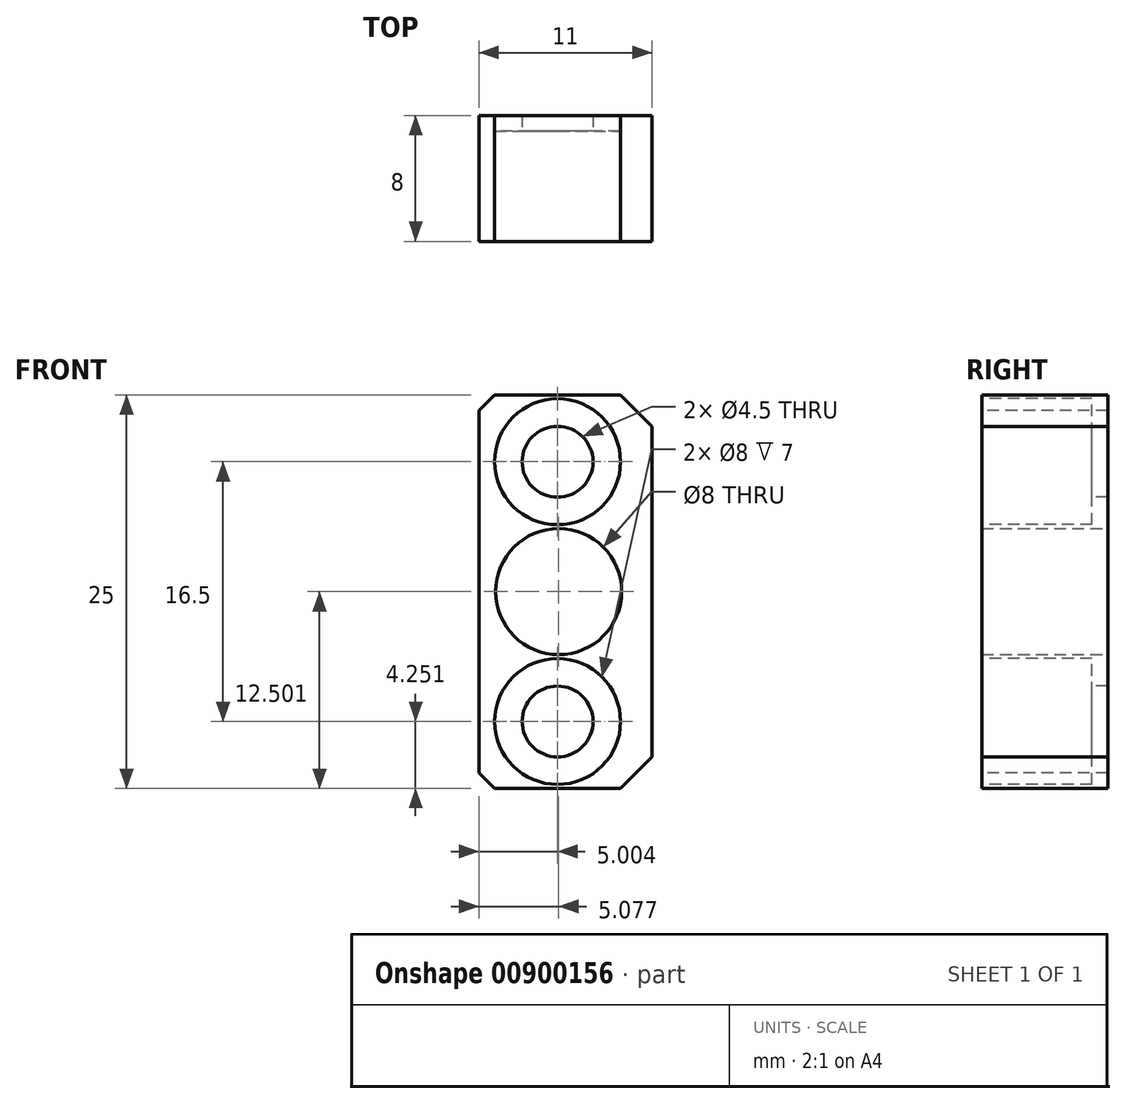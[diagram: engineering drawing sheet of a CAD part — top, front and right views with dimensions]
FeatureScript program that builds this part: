
annotation { "Feature Type Name" : "Feature", "Feature Type Description" : "" }
export const myFeature = defineFeature(function(context is Context, id is Id, definition is map)
    precondition{}
    {
        {
            var Q0;
            Q0=qCreatedBy(makeId("Front.planeOp"),FACE);
            var sketch = newSketch(context, id + "F0", { "sketchPlane" : qUnion([Q0])});
            skLineSegment(sketch, "E0.bottom", {"start": v(-4.19, 15.77) * mm, "end": v(7.81, 15.77) * mm});
            skLineSegment(sketch, "E0.top", {"start": v(-4.19, -9.23) * mm, "end": v(7.81, -9.23) * mm});
            skLineSegment(sketch, "E0.left", {"start": v(-4.19, 15.77) * mm, "end": v(-4.19, -9.23) * mm});
            skLineSegment(sketch, "E0.right", {"start": v(7.81, 15.77) * mm, "end": v(7.81, -9.23) * mm});
            skPoint(sketch, "E1.centerSnap0", {"position": v(1.81, -9.23) * mm});
            skSolve(sketch);
        }
        {
            var Q0;
            Q0=makeQuery(id+"F0.imprint","IMPRINT",FACE,{"disambiguationData":[TD([[makeQuery(id+"F0.imprint","IMPRINT",EDGE,{"derivedFrom":sQuery(id+"F0.wireOp",EDGE,"E0.bottom")}),-1.0]])]});
            extrude(context, id + "F1", {"entities" : qUnion([Q0]), "depth" : 8 * mm, "offsetDistance" : 25 * mm});
        }
        {
            var Q0;
            Q0=makeQuery(id+"F1.opExtrude","SWEPT_EDGE",EDGE,{"disambiguationData":[OSD([sQuery(id+"F0.wireOp",EDGE,"E0.bottom"),sQuery(id+"F0.wireOp",EDGE,"E0.left")])]});
            chamfer(context, id + "F2", {"entities" : qUnion([Q0]), "width" : 2 * mm, "tangentPropagation" : true});
        }
        {
            var Q0;
            Q0=makeQuery(id+"F1.opExtrude","SWEPT_EDGE",EDGE,{"disambiguationData":[OSD([sQuery(id+"F0.wireOp",EDGE,"E0.bottom"),sQuery(id+"F0.wireOp",EDGE,"E0.right")])]});
            var Q1;
            Q1=makeQuery(id+"F1.opExtrude","SWEPT_EDGE",EDGE,{"disambiguationData":[OSD([sQuery(id+"F0.wireOp",EDGE,"E0.top"),sQuery(id+"F0.wireOp",EDGE,"E0.right")])]});
            var Q2;
            Q2=makeQuery(id+"F1.opExtrude","SWEPT_EDGE",EDGE,{"disambiguationData":[OSD([sQuery(id+"F0.wireOp",EDGE,"E0.top"),sQuery(id+"F0.wireOp",EDGE,"E0.left")])]});
            chamfer(context, id + "F3", {"entities" : qUnion([Q0, Q1, Q2]), "width" : 2 * mm, "tangentPropagation" : true});
        }
        {
            var Q0;
            Q0=makeQuery(id+"F1.opExtrude","CAP_FACE",FACE,{"disambiguationData":[OSD([sQuery(id+"F0.wireOp",EDGE,"E0.bottom"),sQuery(id+"F0.wireOp",EDGE,"E0.top"),sQuery(id+"F0.wireOp",EDGE,"E0.left"),sQuery(id+"F0.wireOp",EDGE,"E0.right")])],"isStart":false});
            var sketch = newSketch(context, id + "F4", { "sketchPlane" : qUnion([Q0])});
            skCircle(sketch, "E2", {"center": v(1.81, -4.98) * mm, "radius": 2.25 * mm});
            skPoint(sketch, "E2.centerSnap0", {"position": v(1.81, -9.23) * mm});
            skCircle(sketch, "E3", {"center": v(1.81, 11.52) * mm, "radius": 2.25 * mm});
            skPoint(sketch, "E3.centerSnap0", {"position": v(1.81, 15.77) * mm});
            skSolve(sketch);
        }
        {
            var Q0;
            Q0=qSketchRegion(id+"F4",true);
            extrude(context, id + "F5", {"entities" : qUnion([Q0]), "operationType" : NewBodyOperationType.REMOVE, "oppositeDirection" : true, "depth" : 25 * mm, "offsetDistance" : 25 * mm});
        }
        {
            var Q0;
            Q0=makeQuery(id+"F1.opExtrude","CAP_FACE",FACE,{"disambiguationData":[OSD([sQuery(id+"F0.wireOp",EDGE,"E0.bottom"),sQuery(id+"F0.wireOp",EDGE,"E0.top"),sQuery(id+"F0.wireOp",EDGE,"E0.left"),sQuery(id+"F0.wireOp",EDGE,"E0.right")])],"isStart":false});
            var sketch = newSketch(context, id + "F6", { "sketchPlane" : qUnion([Q0])});
            skCircle(sketch, "E4", {"center": v(1.81, 11.52) * mm, "radius": 4 * mm});
            skCircle(sketch, "E5", {"center": v(1.81, -4.98) * mm, "radius": 4 * mm});
            skSolve(sketch);
        }
        {
            var Q0;
            Q0=qSketchRegion(id+"F6",true);
            extrude(context, id + "F7", {"entities" : qUnion([Q0]), "operationType" : NewBodyOperationType.REMOVE, "oppositeDirection" : true, "depth" : 7 * mm, "offsetDistance" : 25 * mm});
        }
        {
            var Q0;
            Q0=qCreatedBy(makeId("Front.planeOp"),FACE);
            var sketch = newSketch(context, id + "F8", { "sketchPlane" : qUnion([Q0])});
            skCircle(sketch, "E6", {"center": v(1.89, 3.27) * mm, "radius": 4 * mm});
            skSolve(sketch);
        }
        {
            var Q0;
            Q0=makeQuery(id+"F8.imprint","IMPRINT",FACE,{"disambiguationData":[TD([[makeQuery(id+"F8.imprint","IMPRINT",EDGE,{"derivedFrom":sQuery(id+"F8.wireOp",EDGE,"E6")}),1.0]])]});
            extrude(context, id + "F9", {"entities" : qUnion([Q0]), "operationType" : NewBodyOperationType.REMOVE, "depth" : 25 * mm, "offsetDistance" : 25 * mm});
        }
        {
            var Q0;
            Q0=makeQuery(id+"F1.opExtrude","SWEPT_FACE",FACE,{"disambiguationData":[OSD([sQuery(id+"F0.wireOp",EDGE,"E0.left")])]});
            var sketch = newSketch(context, id + "F10", { "sketchPlane" : qUnion([Q0])});
            skLineSegment(sketch, "E7.bottom", {"start": v(0, 16.52) * mm, "end": v(8, 16.52) * mm});
            skLineSegment(sketch, "E7.top", {"start": v(0, -10.74) * mm, "end": v(8, -10.74) * mm});
            skLineSegment(sketch, "E7.left", {"start": v(0, 16.52) * mm, "end": v(0, -10.74) * mm});
            skLineSegment(sketch, "E7.right", {"start": v(8, 16.52) * mm, "end": v(8, -10.74) * mm});
            skSolve(sketch);
        }
        {
            var Q0;
            Q0 = qSketchRegion(id + "F10", true);
            extrude(context, id + "F11", {"entities" : qUnion([Q0]), "operationType" : NewBodyOperationType.REMOVE, "oppositeDirection" : true, "depth" : 1 * mm, "offsetDistance" : 25 * mm});
        }
    });
